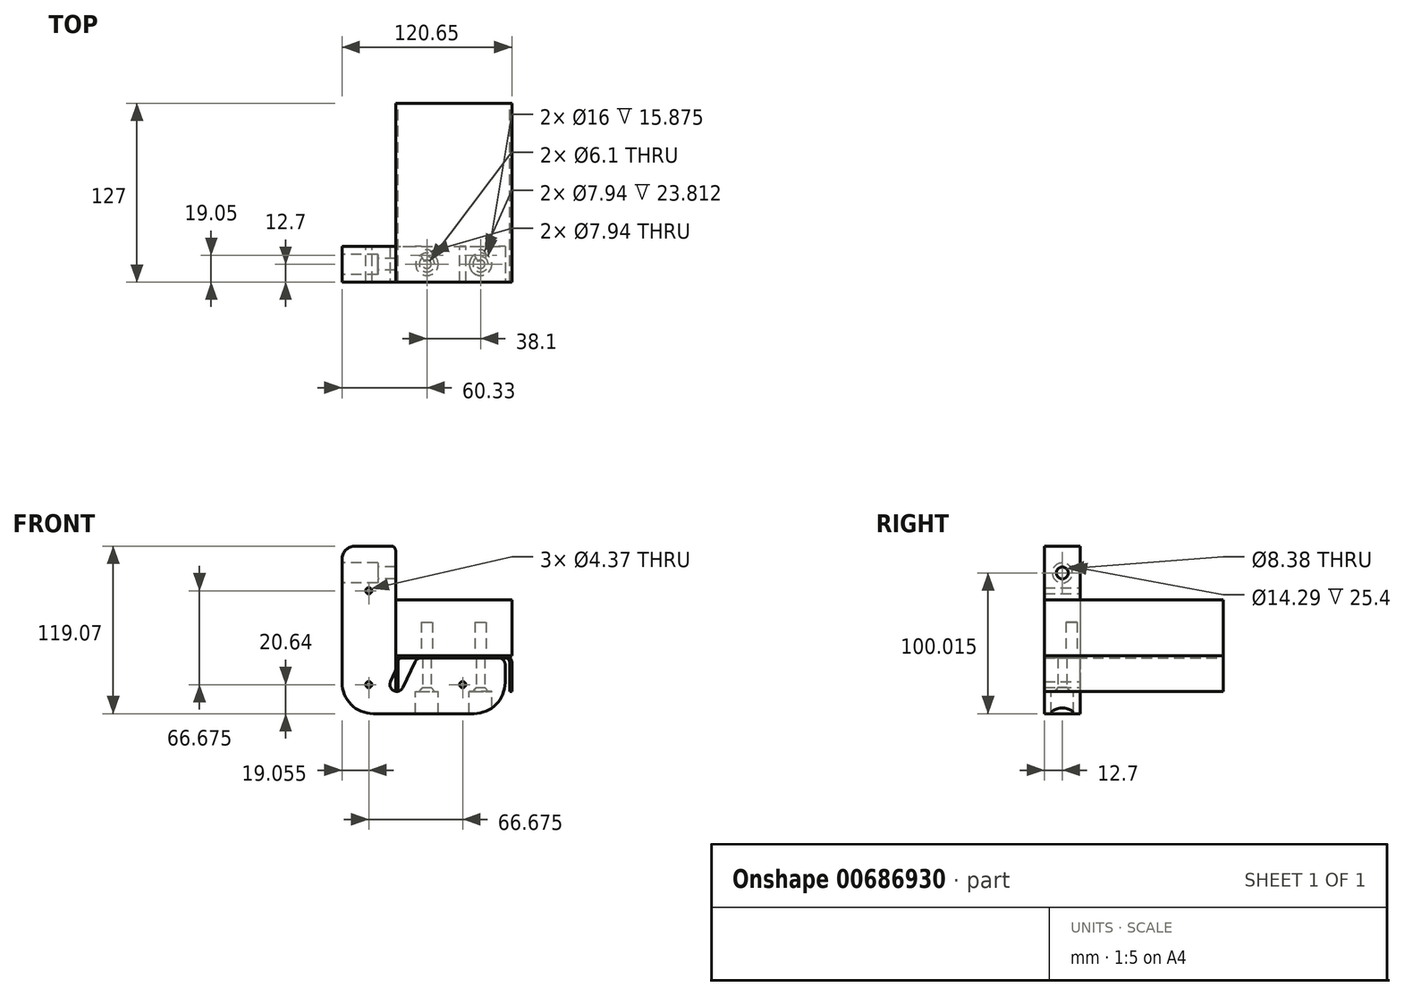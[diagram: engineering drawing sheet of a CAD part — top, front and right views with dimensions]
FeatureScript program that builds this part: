
annotation { "Feature Type Name" : "Feature", "Feature Type Description" : "" }
export const myFeature = defineFeature(function(context is Context, id is Id, definition is map)
    precondition{}
    {
        {
            var Q0;
            Q0=qCreatedBy(makeId("Front.planeOp"),FACE);
            var sketch = newSketch(context, id + "F0", { "sketchPlane" : qUnion([Q0])});
            skLineSegment(sketch, "E0", {"start": v(41.28, -23.81) * mm, "end": v(41.28, -3.17) * mm});
            skLineSegment(sketch, "E1", {"start": v(36.51, 1.59) * mm, "end": v(-36.51, 1.59) * mm});
            skLineSegment(sketch, "E2", {"start": v(-41.27, -3.18) * mm, "end": v(-41.27, -23.81) * mm});
            skLineSegment(sketch, "E3", {"start": v(-41.28, -23.81) * mm, "end": v(-39.69, -23.81) * mm});
            skLineSegment(sketch, "E4", {"start": v(-39.69, -23.81) * mm, "end": v(-39.69, -3.18) * mm});
            skLineSegment(sketch, "E5", {"start": v(-36.51, 0) * mm, "end": v(36.51, 0) * mm});
            skLineSegment(sketch, "E6", {"start": v(39.69, -3.17) * mm, "end": v(39.69, -23.81) * mm});
            skLineSegment(sketch, "E7", {"start": v(39.69, -23.81) * mm, "end": v(41.28, -23.81) * mm});
            skLineSegment(sketch, "E8", {"start": v(0, 0) * mm, "end": v(0, 1.59) * mm, "construction": true});
            skPoint(sketch, "E9.visualSharp", {"position": v(-39.69, 0) * mm});
            skArc(sketch, "E9.filletArc", {"start": v(-36.51, 0) * mm, "mid": v(-38.76, -0.93) * mm, "end": v(-39.69, -3.18) * mm});
            skPoint(sketch, "E10.visualSharp", {"position": v(39.69, 0) * mm});
            skArc(sketch, "E10.filletArc", {"start": v(39.69, -3.17) * mm, "mid": v(38.76, -0.93) * mm, "end": v(36.51, 0) * mm});
            skPoint(sketch, "E11.visualSharp", {"position": v(-41.28, 1.59) * mm});
            skArc(sketch, "E11.filletArc", {"start": v(-36.51, 1.59) * mm, "mid": v(-39.88, 0.2) * mm, "end": v(-41.28, -3.18) * mm});
            skPoint(sketch, "E12.visualSharp", {"position": v(41.28, 1.59) * mm});
            skArc(sketch, "E12.filletArc", {"start": v(41.28, -3.17) * mm, "mid": v(39.88, 0.2) * mm, "end": v(36.51, 1.59) * mm});
            skSolve(sketch);
        }
        {
            var Q0;
            Q0=qSketchRegion(id+"F0",true);
            extrude(context, id + "F1", {"entities" : qUnion([Q0]), "depth" : 127 * mm});
        }
        {
            var Q0;
            Q0=makeQuery(id+"F1.opExtrude","CAP_FACE",FACE,{"disambiguationData":[OSD([sQuery(id+"F0.wireOp",EDGE,"E0"),sQuery(id+"F0.wireOp",EDGE,"E1"),sQuery(id+"F0.wireOp",EDGE,"E2"),sQuery(id+"F0.wireOp",EDGE,"E3"),sQuery(id+"F0.wireOp",EDGE,"E4"),sQuery(id+"F0.wireOp",EDGE,"E5"),sQuery(id+"F0.wireOp",EDGE,"E6"),sQuery(id+"F0.wireOp",EDGE,"E7"),sQuery(id+"F0.wireOp",EDGE,"E9.filletArc"),sQuery(id+"F0.wireOp",EDGE,"E10.filletArc"),sQuery(id+"F0.wireOp",EDGE,"E11.filletArc"),sQuery(id+"F0.wireOp",EDGE,"E12.filletArc")])],"isStart":false});
            var sketch = newSketch(context, id + "F2", { "sketchPlane" : qUnion([Q0])});
            skLineSegment(sketch, "E13.bottom", {"start": v(-41.28, 1.59) * mm, "end": v(41.28, 1.59) * mm});
            skLineSegment(sketch, "E13.top", {"start": v(-41.28, 41.27) * mm, "end": v(41.27, 41.27) * mm});
            skLineSegment(sketch, "E13.left", {"start": v(-41.28, 1.59) * mm, "end": v(-41.28, 41.27) * mm});
            skLineSegment(sketch, "E13.right", {"start": v(41.28, 1.59) * mm, "end": v(41.27, 41.27) * mm});
            skSolve(sketch);
        }
        {
            var Q0;
            Q0=qSketchRegion(id+"F2",true);
            var Q1;
            Q1=makeQuery(id+"F1.opExtrude","CAP_FACE",FACE,{"disambiguationData":[OSD([sQuery(id+"F0.wireOp",EDGE,"E0"),sQuery(id+"F0.wireOp",EDGE,"E1"),sQuery(id+"F0.wireOp",EDGE,"E2"),sQuery(id+"F0.wireOp",EDGE,"E3"),sQuery(id+"F0.wireOp",EDGE,"E4"),sQuery(id+"F0.wireOp",EDGE,"E5"),sQuery(id+"F0.wireOp",EDGE,"E6"),sQuery(id+"F0.wireOp",EDGE,"E7"),sQuery(id+"F0.wireOp",EDGE,"E9.filletArc"),sQuery(id+"F0.wireOp",EDGE,"E10.filletArc"),sQuery(id+"F0.wireOp",EDGE,"E11.filletArc"),sQuery(id+"F0.wireOp",EDGE,"E12.filletArc")])],"isStart":true});
            extrude(context, id + "F3", {"entities" : qUnion([Q0]), "endBound" : BoundingType.UP_TO_SURFACE, "oppositeDirection" : true, "endBoundEntityFace" : qUnion([Q1]), "depth" : 25.4 * mm});
        }
        {
            var Q0;
            Q0=makeQuery(id+"F1.opExtrude","SWEPT_FACE",FACE,{"disambiguationData":[OSD([sQuery(id+"F0.wireOp",EDGE,"E5")])]});
            var sketch = newSketch(context, id + "F4", { "sketchPlane" : qUnion([Q0])});
            skCircle(sketch, "E14", {"center": v(-19.05, 107.95) * mm, "radius": 3.97 * mm});
            skCircle(sketch, "E15", {"center": v(19.05, 107.95) * mm, "radius": 3.97 * mm});
            skLineSegment(sketch, "E16", {"start": v(-19.05, 107.95) * mm, "end": v(-36.51, 107.95) * mm, "construction": true});
            skLineSegment(sketch, "E17", {"start": v(19.05, 107.95) * mm, "end": v(36.51, 107.95) * mm, "construction": true});
            skSolve(sketch);
        }
        {
            var Q0;
            Q0=qSketchRegion(id+"F4",true);
            extrude(context, id + "F5", {"entities" : qUnion([Q0]), "operationType" : NewBodyOperationType.REMOVE, "oppositeDirection" : true, "depth" : 25.4 * mm});
        }
        {
            var Q0;
            Q0=makeQuery(id+"F1.opExtrude","CAP_FACE",FACE,{"disambiguationData":[OSD([sQuery(id+"F0.wireOp",EDGE,"E0"),sQuery(id+"F0.wireOp",EDGE,"E1"),sQuery(id+"F0.wireOp",EDGE,"E2"),sQuery(id+"F0.wireOp",EDGE,"E3"),sQuery(id+"F0.wireOp",EDGE,"E4"),sQuery(id+"F0.wireOp",EDGE,"E5"),sQuery(id+"F0.wireOp",EDGE,"E6"),sQuery(id+"F0.wireOp",EDGE,"E7"),sQuery(id+"F0.wireOp",EDGE,"E9.filletArc"),sQuery(id+"F0.wireOp",EDGE,"E10.filletArc"),sQuery(id+"F0.wireOp",EDGE,"E11.filletArc"),sQuery(id+"F0.wireOp",EDGE,"E12.filletArc")])],"isStart":false});
            var sketch = newSketch(context, id + "F6", { "sketchPlane" : qUnion([Q0])});
            skLineSegment(sketch, "E18", {"start": v(-41.28, 79.38) * mm, "end": v(-79.38, 79.38) * mm});
            skLineSegment(sketch, "E19", {"start": v(-79.38, 79.38) * mm, "end": v(-79.38, -39.69) * mm});
            skLineSegment(sketch, "E20", {"start": v(-79.37, -39.69) * mm, "end": v(36.51, -39.69) * mm});
            skLineSegment(sketch, "E21", {"start": v(36.51, -39.69) * mm, "end": v(36.51, -4.76) * mm});
            skLineSegment(sketch, "E22", {"start": v(31.75, 0) * mm, "end": v(-26.2, 0) * mm});
            skPoint(sketch, "E23.visualSharp", {"position": v(36.51, 0) * mm});
            skArc(sketch, "E23.filletArc", {"start": v(36.51, -4.76) * mm, "mid": v(35.12, -1.4) * mm, "end": v(31.75, 0) * mm});
            skCircle(sketch, "E24", {"center": v(-19.05, -8.8) * mm, "radius": 3.97 * mm, "construction": true});
            skCircle(sketch, "E25", {"center": v(19.05, -8.8) * mm, "radius": 3.97 * mm, "construction": true});
            skLineSegment(sketch, "E26", {"start": v(-19.05, -8.8) * mm, "end": v(19.05, -8.8) * mm, "construction": true});
            skLineSegment(sketch, "E27", {"start": v(0, -8.8) * mm, "end": v(0, 0) * mm, "construction": true});
            skLineSegment(sketch, "E28", {"start": v(-19.05, -8.8) * mm, "end": v(-23.02, -8.8) * mm, "construction": true});
            skLineSegment(sketch, "E29", {"start": v(-41.28, -9.1) * mm, "end": v(-41.28, 79.38) * mm});
            skLineSegment(sketch, "E30", {"start": v(-36.11, -21.1) * mm, "end": v(-26.2, 0) * mm});
            skLineSegment(sketch, "E31", {"start": v(-44.88, -17.06) * mm, "end": v(-41.28, -9.1) * mm});
            skArc(sketch, "E32", {"start": v(-44.88, -17.06) * mm, "mid": v(-42.5, -23.43) * mm, "end": v(-36.11, -21.1) * mm});
            skPoint(sketch, "E33", {"position": v(-41.27, -13.5) * mm});
            skCircle(sketch, "E34", {"center": v(-36.82, -11.11) * mm, "radius": 4.89 * mm, "construction": true});
            skSolve(sketch);
        }
        {
            var Q0;
            {var subQ6=sQuery(id+"F6.wireOp",EDGE,"E18");Q0=makeQuery(id+"F6.imprint","IMPRINT",FACE,{"disambiguationData":[TD([[makeQuery(id+"F6.imprint","IMPRINT",EDGE,{"derivedFrom":subQ6}),1.0]])]});}
            extrude(context, id + "F7", {"entities" : qUnion([Q0]), "oppositeDirection" : true, "depth" : 25.4 * mm});
        }
        {
            var Q0;
            Q0=makeQuery(id+"F7.opExtrude","SWEPT_EDGE",EDGE,{"disambiguationData":[OSD([sQuery(id+"F6.wireOp",EDGE,"E19"),sQuery(id+"F6.wireOp",EDGE,"E20")])]});
            var Q1;
            Q1=makeQuery(id+"F7.opExtrude","SWEPT_EDGE",EDGE,{"disambiguationData":[OSD([sQuery(id+"F6.wireOp",EDGE,"E20"),sQuery(id+"F6.wireOp",EDGE,"E21")])]});
            fillet(context, id + "F8", {"entities" : qUnion([Q0, Q1]), "radius" : 22.22 * mm, "tangentPropagation" : true, "allowEdgeOverflow" : false});
        }
        {
            var Q0;
            Q0=makeQuery(id+"F7.opExtrude","SWEPT_FACE",FACE,{"disambiguationData":[OSD([sQuery(id+"F6.wireOp",EDGE,"E20")])]});
            cPlane(context, id + "F9", {"entities" : qUnion([Q0]), "cplaneType" : CPlaneType.OFFSET, "offset" : 15.88 * mm, "oppositeDirection" : true, "width" : 152.4 * mm, "height" : 152.4 * mm});
        }
        {
            var Q0;
            Q0=qCreatedBy(id+"F9.planeOp",FACE);
            var sketch = newSketch(context, id + "F10", { "sketchPlane" : qUnion([Q0])});
            skPoint(sketch, "E35", {"position": v(-19.05, 114.3) * mm});
            skPoint(sketch, "E36", {"position": v(19.05, 114.3) * mm});
            skLineSegment(sketch, "E37", {"start": v(19.05, 114.3) * mm, "end": v(19.05, 107.95) * mm, "construction": true});
            skLineSegment(sketch, "E38", {"start": v(-19.05, 114.3) * mm, "end": v(-19.05, 107.95) * mm, "construction": true});
            skLineSegment(sketch, "E39", {"start": v(-19.05, 114.3) * mm, "end": v(-57.15, 114.3) * mm, "construction": true});
            skPoint(sketch, "E40", {"position": v(-60.33, 114.3) * mm});
            skCircle(sketch, "E41", {"center": v(-19.05, 114.3) * mm, "radius": 8 * mm});
            skCircle(sketch, "E42", {"center": v(19.05, 114.3) * mm, "radius": 8 * mm});
            skSolve(sketch);
        }
        {
            var Q0;
            Q0=qSketchRegion(id+"F10",true);
            extrude(context, id + "F11", {"entities" : qUnion([Q0]), "operationType" : NewBodyOperationType.REMOVE, "depth" : 25.4 * mm});
        }
        {
            var Q0;
            Q0=sQuery(id+"F10.wireOp",VERTEX,"E35");
            var Q1;
            Q1=sQuery(id+"F10.wireOp",VERTEX,"E36");
            var Q2;
            Q2=makeQuery(id+"F7.opExtrude","SWEPT_BODY",BODY,{"disambiguationData":[OSD([sQuery(id+"F6.wireOp",EDGE,"E18"),sQuery(id+"F6.wireOp",EDGE,"E19"),sQuery(id+"F6.wireOp",EDGE,"E20"),sQuery(id+"F6.wireOp",EDGE,"E21"),sQuery(id+"F6.wireOp",EDGE,"E22"),sQuery(id+"F6.wireOp",EDGE,"VCN7EzUT-UCgr-9Dl2-yQ6i-yJvqr16Mm8If"),sQuery(id+"F6.wireOp",EDGE,"28iwqmir-5wwE-XKHo-pBXU-8pbr5TsYityO"),sQuery(id+"F6.wireOp",EDGE,"E23.filletArc"),sQuery(id+"F6.wireOp",EDGE,"5D1ydIdo-Vbug-DlCE-rGqy-j11egtTWor9N"),sQuery(id+"F6.wireOp",EDGE,"fc85a2f7-f7e6-4432-93fa-4e404d59246a.filletArc")])]});
            hole(context, id + "F12", {"style" : HoleStyle.C_SINK, "endStyle" : HoleEndStyle.THROUGH, "holeDiameter" : 6.1 * mm, "cSinkDiameter" : 10.92 * mm, "cSinkAngle" : 82 * degree, "locations" : qUnion([Q0, Q1]), "scope" : qUnion([Q2]), "isTappedThrough" : true});
        }
        {
            var Q0;
            Q0=makeQuery(id+"F7.opExtrude","SWEPT_EDGE",EDGE,{"disambiguationData":[OSD([sQuery(id+"F6.wireOp",EDGE,"E18"),sQuery(id+"F6.wireOp",EDGE,"E29")])]});
            fillet(context, id + "F13", {"entities" : qUnion([Q0]), "radius" : 3.17 * mm, "tangentPropagation" : true, "allowEdgeOverflow" : false});
        }
        {
            var Q0;
            Q0=makeQuery(id+"F7.opExtrude","SWEPT_EDGE",EDGE,{"disambiguationData":[OSD([sQuery(id+"F6.wireOp",EDGE,"E18"),sQuery(id+"F6.wireOp",EDGE,"E19")])]});
            fillet(context, id + "F14", {"entities" : qUnion([Q0]), "radius" : 9.52 * mm, "tangentPropagation" : true, "allowEdgeOverflow" : false});
        }
        {
            var Q0;
            Q0=makeQuery(id+"F7.opExtrude","SWEPT_FACE",FACE,{"disambiguationData":[OSD([sQuery(id+"F6.wireOp",EDGE,"E19")])]});
            var sketch = newSketch(context, id + "F15", { "sketchPlane" : qUnion([Q0])});
            skPoint(sketch, "E43", {"position": v(114.3, 60.33) * mm});
            skLineSegment(sketch, "E44", {"start": v(101.6, 60.33) * mm, "end": v(127, 60.33) * mm, "construction": true});
            skSolve(sketch);
        }
        {
            var Q0;
            Q0=sQuery(id+"F15.wireOp",VERTEX,"E43");
            var Q1;
            Q1=makeQuery(id+"F7.opExtrude","SWEPT_BODY",BODY,{"disambiguationData":[OSD([sQuery(id+"F6.wireOp",EDGE,"E18"),sQuery(id+"F6.wireOp",EDGE,"E19"),sQuery(id+"F6.wireOp",EDGE,"E20"),sQuery(id+"F6.wireOp",EDGE,"E21"),sQuery(id+"F6.wireOp",EDGE,"E22"),sQuery(id+"F6.wireOp",EDGE,"E23.filletArc"),sQuery(id+"F6.wireOp",EDGE,"E29"),sQuery(id+"F6.wireOp",EDGE,"E30"),sQuery(id+"F6.wireOp",EDGE,"E31"),sQuery(id+"F6.wireOp",EDGE,"E32")])]});
            hole(context, id + "F16", {"style" : HoleStyle.C_BORE, "endStyle" : HoleEndStyle.THROUGH, "holeDiameter" : 8.38 * mm, "cBoreDiameter" : 14.29 * mm, "cBoreDepth" : 25.4 * mm, "locations" : qUnion([Q0]), "scope" : qUnion([Q1]), "isTappedThrough" : true});
        }
        {
            var Q0;
            Q0=makeQuery(id+"F7.opExtrude","SWEPT_EDGE",EDGE,{"disambiguationData":[OSD([sQuery(id+"F0.wireOp",EDGE,"E2"),sQuery(id+"F6.wireOp",EDGE,"E29"),sQuery(id+"F6.wireOp",EDGE,"E31")])]});
            var Q1;
            Q1=makeQuery(id+"F7.opExtrude","SWEPT_EDGE",EDGE,{"disambiguationData":[OSD([sQuery(id+"F0.wireOp",EDGE,"E5"),sQuery(id+"F6.wireOp",EDGE,"E22"),sQuery(id+"F6.wireOp",EDGE,"E30")])]});
            fillet(context, id + "F17", {"entities" : qUnion([Q0, Q1]), "radius" : 5.08 * mm, "tangentPropagation" : true, "allowEdgeOverflow" : false});
        }
        {
            var Q0;
            Q0=makeQuery(id+"F7.opExtrude","CAP_FACE",FACE,{"disambiguationData":[OSD([sQuery(id+"F6.wireOp",EDGE,"E18"),sQuery(id+"F6.wireOp",EDGE,"E19"),sQuery(id+"F6.wireOp",EDGE,"E20"),sQuery(id+"F6.wireOp",EDGE,"E21"),sQuery(id+"F6.wireOp",EDGE,"E22"),sQuery(id+"F6.wireOp",EDGE,"E23.filletArc"),sQuery(id+"F6.wireOp",EDGE,"E29"),sQuery(id+"F6.wireOp",EDGE,"E30"),sQuery(id+"F6.wireOp",EDGE,"E31"),sQuery(id+"F6.wireOp",EDGE,"E32")])],"isStart":false});
            var sketch = newSketch(context, id + "F18", { "sketchPlane" : qUnion([Q0])});
            skCircle(sketch, "E45", {"center": v(60.33, 47.62) * mm, "radius": 2.18 * mm});
            skCircle(sketch, "E46", {"center": v(60.33, -19.05) * mm, "radius": 2.18 * mm});
            skCircle(sketch, "E47", {"center": v(-6.35, -19.05) * mm, "radius": 2.18 * mm});
            skLineSegment(sketch, "E48", {"start": v(41.28, 20.33) * mm, "end": v(79.38, 20.33) * mm, "construction": true});
            skLineSegment(sketch, "E49", {"start": v(60.33, 20.33) * mm, "end": v(60.33, -19.05) * mm, "construction": true});
            skSolve(sketch);
        }
        {
            var Q0;
            Q0=qSketchRegion(id+"F18",true);
            extrude(context, id + "F19", {"entities" : qUnion([Q0]), "operationType" : NewBodyOperationType.REMOVE, "endBound" : BoundingType.THROUGH_ALL, "oppositeDirection" : true, "depth" : 25.4 * mm});
        }
    });
